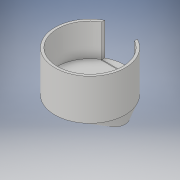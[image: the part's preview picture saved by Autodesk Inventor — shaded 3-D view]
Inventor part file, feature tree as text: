
AUTODESK INVENTOR PART (.ipt)
format: ipt  version: 2019 (Build 230136000, 136)  size: 249,344 bytes
history: native  units: mm
features: sketch x6, extrude x4, fillet x3, loft x2, other x2, plane x1
ambient origin geometry x8: Origin, YZ Plane, XZ Plane, XY Plane, X Axis, Y Axis, Z Axis, Center Point
bodies: Solid1 (feature_tree)
feature tree (18):
  extrude  "Extrusion1"  Depth=86.0mm
  extrude  "Extrusion2"  Depth=1.0mm
  extrude  "Extrusion3"  Depth=40.0mm
  sketch  "Sketch9"  dims[d7=80.0mm d8=10.0mm d9=0.0mm]
  plane  "Work Plane2"
  loft  "Loft1"
  extrude  "Extrusion6"  Depth=40.0mm
  loft  "Loft2"
  fillet  "Fillet1"  [1 undecoded]
  fillet  "Fillet2"  Radius=20.0mm
  fillet  "Fillet3"  Radius=20.0mm
  sketch  "Sketch1"  dims[d0=80.0mm d1=86.0mm]
  sketch  "Sketch2"  dims[d2=40.0mm d3=0.0mm d4=1.0mm]
  sketch  "Sketch3"  dims[d5=1.0mm d6=40.0mm]
  sketch  "Sketch10"  dims[d10=10.0mm d11=0.0mm d21=40.0mm]
  sketch  "Sketch11"  dims[d22=26.0mm d23=0.0mm d24=90.0deg d25=0.0mm d26=90.0deg d27=20.0mm d28=20.0mm d29=0.0mm d30=0.0mm d31=90.0deg d32=0.0mm d33=90.0deg d34=10.0mm d35=10.0mm d36=86.0mm d37=86.0mm d38=43.0mm d39=86.0mm d40=5.0mm]
  other  "Edges1"
  other  "Edges2"
note: 1 required parameter value undecoded (feature->parameter linkage not recoverable at this tier; creation-order binding heuristic only, values carry confidence <= 0.55)
